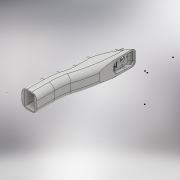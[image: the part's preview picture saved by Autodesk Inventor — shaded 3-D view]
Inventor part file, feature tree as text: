
AUTODESK INVENTOR PART (.ipt)
format: ipt  version: 2017 (Build 210142000, 142)  size: 1,185,280 bytes
history: native  units: mm
features: sketch x37, extrude x31, projected_geometry x21, fillet x2, sweep x1
ambient origin geometry x8: Origin, YZ Plane, XZ Plane, XY Plane, X Axis, Y Axis, Z Axis, Center Point
bodies: Solid1 (feature_tree)
feature tree (92):
  extrude  "Extrusion1"  Depth=35.0mm
  extrude  "Extrusion2"  Depth=9.0mm TaperAngle=0.0deg
  extrude  "Extrusion6"  Depth=70.0mm TaperAngle=0.0deg
  extrude  "Extrusion9"  TaperAngle=90.0deg  [1 undecoded]
  fillet  "Fillet1"  Radius=100.0mm
  extrude  "Extrusion10"  Depth=25.0mm TaperAngle=0.0deg
  extrude  "Extrusion11"  Depth=18.0mm TaperAngle=0.0deg
  extrude  "Extrusion12"  Depth=18.0mm TaperAngle=0.0deg
  extrude  "Extrusion13"  Depth=12.0mm
  extrude  "Extrusion14"  Depth=4.0mm TaperAngle=0.0deg
  extrude  "Extrusion15"  Depth=2.0mm
  extrude  "Extrusion16"  Depth=2.0mm
  extrude  "Extrusion17"  Depth=15.0mm TaperAngle=0.0deg
  extrude  "Extrusion18"  Depth=5.0mm
  extrude  "Extrusion19"  Depth=4.0mm TaperAngle=0.0deg
  extrude  "Extrusion20"  Depth=3.0mm
  extrude  "Extrusion21"  Depth=5.0mm
  extrude  "Extrusion22"  Depth=3.0mm
  fillet  "Fillet2"  Radius=15.0mm
  extrude  "Extrusion23"  Depth=0.1mm TaperAngle=0.0deg
  extrude  "Extrusion24"  Depth=3.958081mm
  extrude  "Extrusion25"  Depth=30.0mm
  extrude  "Extrusion26"  Depth=40.0mm TaperAngle=0.0deg
  extrude  "Extrusion27"  Depth=0.5mm
  extrude  "Extrusion28"  Depth=4.0mm TaperAngle=0.0deg
  extrude  "Extrusion29"  Depth=0.5mm TaperAngle=0.0deg
  sketch  "Sketch42"  dims[d131=4.0mm d132=0.0mm d133=2.0mm d134=0.0mm]
  extrude  "Extrusion30"  Depth=2.0mm TaperAngle=0.0deg
  extrude  "Extrusion31"  Depth=8.0mm TaperAngle=0.0deg
  extrude  "Extrusion32"  Depth=1.5mm
  sketch  "Sketch46"
  sketch  "Sketch47"
  extrude  "Extrusion33"  TaperAngle=0.0deg  [1 undecoded]
  extrude  "Extrusion34"  [1 undecoded]
  extrude  "Extrusion35"  [1 undecoded]
  extrude  "Extrusion36"  [1 undecoded]
  sketch  "Sketch52"
  sketch  "Sketch53"
  sweep  "Sweep1"
  sketch  "Sketch1"  dims[d0=63.0mm d1=0.0mm d2=35.0mm]
  sketch  "Sketch3"  dims[d3=150.0mm d4=9.0mm d5=0.0mm]
  sketch  "Sketch12"  dims[d30=250.0mm d31=0.0mm d48=70.0mm d49=0.0mm]
  sketch  "Sketch17"  dims[d50=8.0mm d51=90.0deg d52=100.0mm d53=0.0mm]
  sketch  "Sketch19"  dims[d54=100.0mm d55=0.0mm d56=25.0mm d57=0.0mm]
  sketch  "Sketch20"  dims[d58=20.0mm d59=0.0mm d60=18.0mm d61=0.0mm]
  sketch  "Sketch21"  dims[d71=25.0mm d72=0.0mm d73=18.0mm d74=0.0mm]
  projected_geometry  "Projected Loop4"
  sketch  "Sketch22"  dims[d75=7.0mm d76=0.0mm d77=12.0mm]
  projected_geometry  "Projected Loop5"
  sketch  "Sketch23"  dims[d78=6.0mm d79=4.0mm d80=0.0mm]
  projected_geometry  "Projected Loop6"
  sketch  "Sketch24"  dims[d81=4.0mm d82=0.0mm d83=2.0mm]
  projected_geometry  "Projected Loop7"
  sketch  "Sketch25"  dims[d84=2.0mm d85=2.0mm]
  sketch  "Sketch26"  dims[d86=2.0mm d87=15.0mm d88=0.0mm]
  projected_geometry  "Projected Loop8"
  sketch  "Sketch27"  dims[d89=5.0mm d90=5.0mm]
  sketch  "Sketch28"  dims[d91=5.0mm d92=4.0mm d93=0.0mm]
  sketch  "Sketch30"  dims[d94=2.0mm d96=3.0mm]
  projected_geometry  "Projected Loop9"
  projected_geometry  "Projected Loop10"
  projected_geometry  "Projected Loop11"
  projected_geometry  "Projected Loop12"
  sketch  "Sketch31"  dims[d97=8.0mm d98=0.0mm d99=5.0mm]
  sketch  "Sketch32"  dims[d100=3.0mm d101=3.0mm d102=15.0mm d103=0.0mm]
  sketch  "Sketch33"  dims[d104=40.0mm d105=0.0mm d106=0.1mm d107=0.0mm]
  sketch  "Sketch34"  dims[d108=4.0mm d109=0.0mm d110=3.958081mm]
  projected_geometry  "Projected Loop13"
  sketch  "Sketch35"  dims[d111=30.0mm d112=30.0mm]
  projected_geometry  "Projected Loop14"
  sketch  "Sketch36"  dims[d113=7.0mm d114=40.0mm d115=0.0mm]
  sketch  "Sketch37"  dims[d116=0.5mm d117=0.5mm]
  sketch  "Sketch40"  dims[d118=15.0mm d119=0.0mm d125=4.0mm d126=0.0mm]
  sketch  "Sketch41"  dims[d127=4.0mm d128=0.0mm d129=0.5mm d130=0.0mm]
  projected_geometry  "Projected Loop16"
  sketch  "Sketch43"  dims[d135=1.0mm d136=0.0mm d137=8.0mm d138=0.0mm]
  projected_geometry  "Projected Loop17"
  sketch  "Sketch44"  dims[d139=8.0mm d140=0.0mm d141=1.5mm]
  projected_geometry  "Projected Loop18"
  sketch  "Sketch45"  dims[d144=1.5mm d145=0.0mm d146=0.0mm]
  projected_geometry  "Projected Loop19"
  projected_geometry  "Projected Loop20"
  sketch  "Sketch48"
  projected_geometry  "Projected Loop21"
  sketch  "Sketch49"
  projected_geometry  "Projected Loop22"
  sketch  "Sketch50"
  projected_geometry  "Projected Loop23"
  projected_geometry  "Projected Loop24"
  sketch  "Sketch51"
  projected_geometry  "Projected Loop25"
  sketch  "3D Sketch1"
note: 5 required parameter values undecoded (feature->parameter linkage not recoverable at this tier; creation-order binding heuristic only, values carry confidence <= 0.55)
